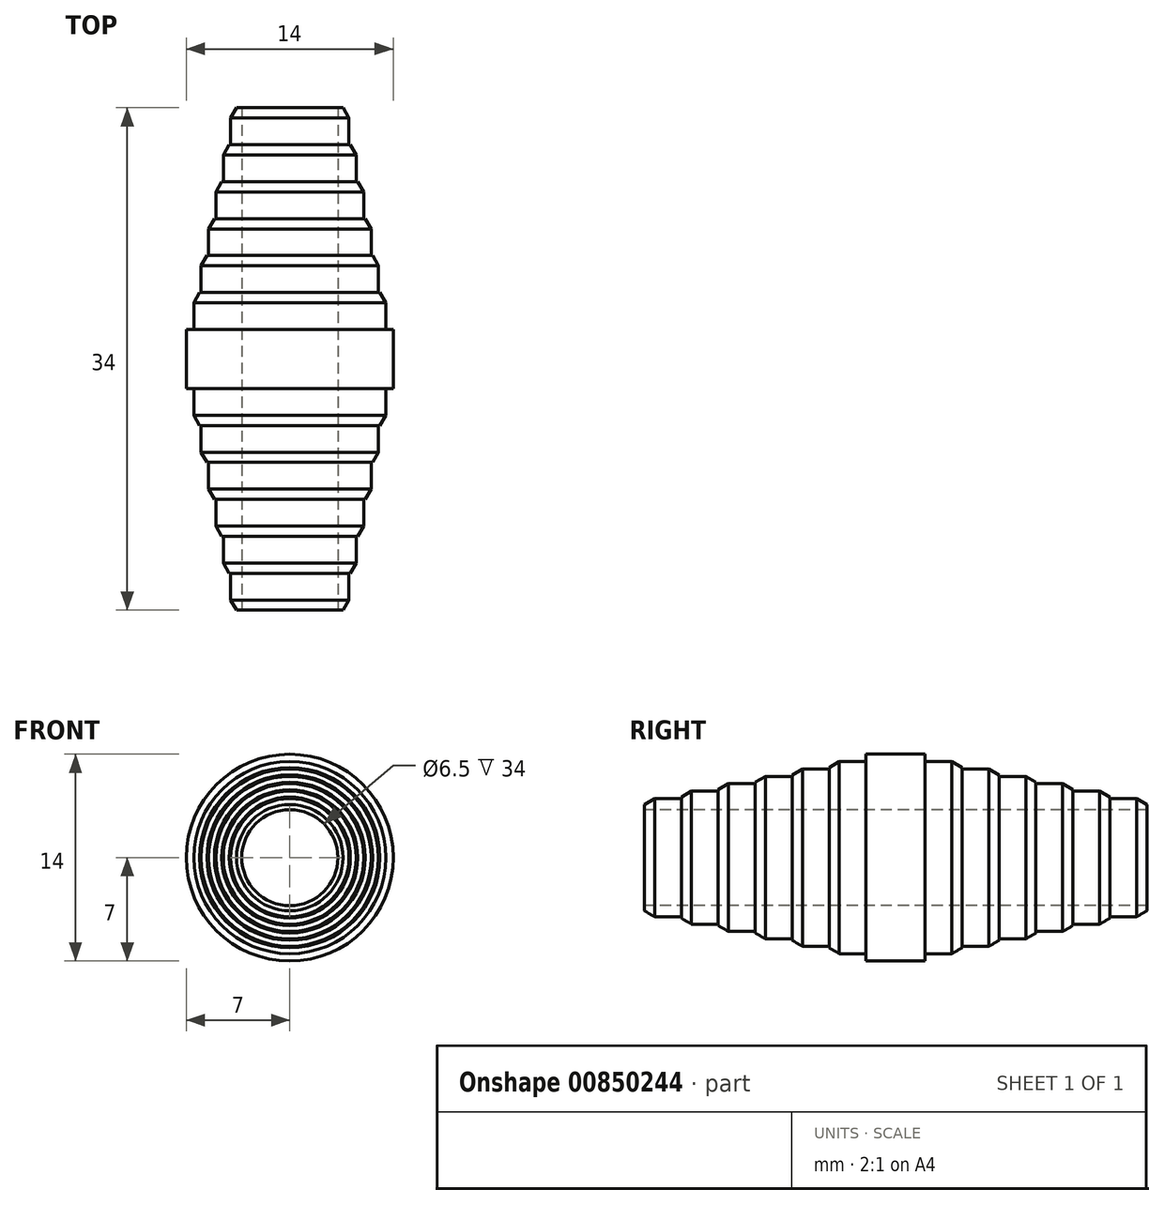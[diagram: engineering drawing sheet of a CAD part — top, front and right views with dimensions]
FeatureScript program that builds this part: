
annotation { "Feature Type Name" : "Feature", "Feature Type Description" : "" }
export const myFeature = defineFeature(function(context is Context, id is Id, definition is map)
    precondition{}
    {
        {
            var Q0;
            Q0=qCreatedBy(makeId("Front.planeOp"),FACE);
            var sketch = newSketch(context, id + "F0", { "sketchPlane" : qUnion([Q0])});
            skCircle(sketch, "E0", {"center": v(0, 0) * mm, "radius": 7 * mm});
            skCircle(sketch, "E1.0", {"center": v(0, 0) * mm, "radius": 6.5 * mm});
            skCircle(sketch, "E2.0", {"center": v(0, 0) * mm, "radius": 6 * mm});
            skCircle(sketch, "E3.0", {"center": v(0, 0) * mm, "radius": 5.5 * mm});
            skCircle(sketch, "E4.0", {"center": v(0, 0) * mm, "radius": 5 * mm});
            skCircle(sketch, "E5.0", {"center": v(0, 0) * mm, "radius": 4.5 * mm});
            skCircle(sketch, "E6.0", {"center": v(0, 0) * mm, "radius": 4 * mm});
            skSolve(sketch);
        }
        {
            var Q0;
            Q0=makeQuery(id+"F0.imprint","IMPRINT",FACE,{"disambiguationData":[TD([[makeQuery(id+"F0.imprint","IMPRINT",EDGE,{"derivedFrom":sQuery(id+"F0.wireOp",EDGE,"E0")}),1.0]])]});
            var Q1;
            Q1=makeQuery(id+"F0.imprint","IMPRINT",FACE,{"disambiguationData":[TD([[makeQuery(id+"F0.imprint","IMPRINT",EDGE,{"derivedFrom":sQuery(id+"F0.wireOp",EDGE,"E1.0")}),1.0]])]});
            var Q2;
            Q2=makeQuery(id+"F0.imprint","IMPRINT",FACE,{"disambiguationData":[TD([[makeQuery(id+"F0.imprint","IMPRINT",EDGE,{"derivedFrom":sQuery(id+"F0.wireOp",EDGE,"E2.0")}),1.0]])]});
            var Q3;
            Q3=makeQuery(id+"F0.imprint","IMPRINT",FACE,{"disambiguationData":[TD([[makeQuery(id+"F0.imprint","IMPRINT",EDGE,{"derivedFrom":sQuery(id+"F0.wireOp",EDGE,"E3.0")}),1.0]])]});
            var Q4;
            Q4=makeQuery(id+"F0.imprint","IMPRINT",FACE,{"disambiguationData":[TD([[makeQuery(id+"F0.imprint","IMPRINT",EDGE,{"derivedFrom":sQuery(id+"F0.wireOp",EDGE,"E4.0")}),1.0]])]});
            var Q5;
            Q5=makeQuery(id+"F0.imprint","IMPRINT",FACE,{"disambiguationData":[TD([[makeQuery(id+"F0.imprint","IMPRINT",EDGE,{"derivedFrom":sQuery(id+"F0.wireOp",EDGE,"E5.0")}),1.0]])]});
            var Q6;
            Q6=makeQuery(id+"F0.imprint","IMPRINT",FACE,{"disambiguationData":[TD([[makeQuery(id+"F0.imprint","IMPRINT",EDGE,{"derivedFrom":sQuery(id+"F0.wireOp",EDGE,"E6.0")}),1.0]])]});
            extrude(context, id + "F1", {"entities" : qUnion([Q0, Q1, Q2, Q3, Q4, Q5, Q6]), "depth" : 2 * mm, "offsetDistance" : 25 * mm});
        }
        {
            var Q0;
            Q0=makeQuery(id+"F0.imprint","IMPRINT",FACE,{"disambiguationData":[TD([[makeQuery(id+"F0.imprint","IMPRINT",EDGE,{"derivedFrom":sQuery(id+"F0.wireOp",EDGE,"E1.0")}),1.0]])]});
            var Q1;
            Q1=makeQuery(id+"F0.imprint","IMPRINT",FACE,{"disambiguationData":[TD([[makeQuery(id+"F0.imprint","IMPRINT",EDGE,{"derivedFrom":sQuery(id+"F0.wireOp",EDGE,"E2.0")}),1.0]])]});
            var Q2;
            Q2=makeQuery(id+"F0.imprint","IMPRINT",FACE,{"disambiguationData":[TD([[makeQuery(id+"F0.imprint","IMPRINT",EDGE,{"derivedFrom":sQuery(id+"F0.wireOp",EDGE,"E3.0")}),1.0]])]});
            var Q3;
            Q3=makeQuery(id+"F0.imprint","IMPRINT",FACE,{"disambiguationData":[TD([[makeQuery(id+"F0.imprint","IMPRINT",EDGE,{"derivedFrom":sQuery(id+"F0.wireOp",EDGE,"E4.0")}),1.0]])]});
            var Q4;
            Q4=makeQuery(id+"F0.imprint","IMPRINT",FACE,{"disambiguationData":[TD([[makeQuery(id+"F0.imprint","IMPRINT",EDGE,{"derivedFrom":sQuery(id+"F0.wireOp",EDGE,"E5.0")}),1.0]])]});
            var Q5;
            Q5=makeQuery(id+"F0.imprint","IMPRINT",FACE,{"disambiguationData":[TD([[makeQuery(id+"F0.imprint","IMPRINT",EDGE,{"derivedFrom":sQuery(id+"F0.wireOp",EDGE,"E6.0")}),1.0]])]});
            var Q6;
            Q6=makeQuery(id+"F1.opExtrude","CAP_FACE",FACE,{"disambiguationData":[OSD([sQuery(id+"F0.wireOp",EDGE,"E0"),sQuery(id+"F0.wireOp",EDGE,"E6.0")])],"isStart":false});
            extrude(context, id + "F2", {"entities" : qUnion([Q0, Q1, Q2, Q3, Q4, Q5]), "operationType" : NewBodyOperationType.ADD, "endBound" : BoundingType.UP_TO_SURFACE, "depth" : 25 * mm, "endBoundEntityFace" : qUnion([Q6]), "hasOffset" : true, "offsetDistance" : -2.5 * mm});
        }
        {
            var Q0;
            Q0=makeQuery(id+"F0.imprint","IMPRINT",FACE,{"disambiguationData":[TD([[makeQuery(id+"F0.imprint","IMPRINT",EDGE,{"derivedFrom":sQuery(id+"F0.wireOp",EDGE,"E6.0")}),1.0]])]});
            var Q1;
            Q1=makeQuery(id+"F0.imprint","IMPRINT",FACE,{"disambiguationData":[TD([[makeQuery(id+"F0.imprint","IMPRINT",EDGE,{"derivedFrom":sQuery(id+"F0.wireOp",EDGE,"E5.0")}),1.0]])]});
            var Q2;
            Q2=makeQuery(id+"F0.imprint","IMPRINT",FACE,{"disambiguationData":[TD([[makeQuery(id+"F0.imprint","IMPRINT",EDGE,{"derivedFrom":sQuery(id+"F0.wireOp",EDGE,"E4.0")}),1.0]])]});
            var Q3;
            Q3=makeQuery(id+"F0.imprint","IMPRINT",FACE,{"disambiguationData":[TD([[makeQuery(id+"F0.imprint","IMPRINT",EDGE,{"derivedFrom":sQuery(id+"F0.wireOp",EDGE,"E3.0")}),1.0]])]});
            var Q4;
            Q4=makeQuery(id+"F0.imprint","IMPRINT",FACE,{"disambiguationData":[TD([[makeQuery(id+"F0.imprint","IMPRINT",EDGE,{"derivedFrom":sQuery(id+"F0.wireOp",EDGE,"E2.0")}),1.0]])]});
            var Q5;
            Q5=makeQuery(id+"F2.opExtrude","CAP_FACE",FACE,{"disambiguationData":[OSD([sQuery(id+"F0.wireOp",EDGE,"E1.0")])],"isStart":false});
            extrude(context, id + "F3", {"entities" : qUnion([Q0, Q1, Q2, Q3, Q4]), "operationType" : NewBodyOperationType.ADD, "endBound" : BoundingType.UP_TO_SURFACE, "depth" : 25 * mm, "endBoundEntityFace" : qUnion([Q5]), "hasOffset" : true, "offsetDistance" : -2.5 * mm});
        }
        {
            var Q0;
            Q0=makeQuery(id+"F0.imprint","IMPRINT",FACE,{"disambiguationData":[TD([[makeQuery(id+"F0.imprint","IMPRINT",EDGE,{"derivedFrom":sQuery(id+"F0.wireOp",EDGE,"E6.0")}),1.0]])]});
            var Q1;
            Q1=makeQuery(id+"F0.imprint","IMPRINT",FACE,{"disambiguationData":[TD([[makeQuery(id+"F0.imprint","IMPRINT",EDGE,{"derivedFrom":sQuery(id+"F0.wireOp",EDGE,"E5.0")}),1.0]])]});
            var Q2;
            Q2=makeQuery(id+"F0.imprint","IMPRINT",FACE,{"disambiguationData":[TD([[makeQuery(id+"F0.imprint","IMPRINT",EDGE,{"derivedFrom":sQuery(id+"F0.wireOp",EDGE,"E4.0")}),1.0]])]});
            var Q3;
            Q3=makeQuery(id+"F0.imprint","IMPRINT",FACE,{"disambiguationData":[TD([[makeQuery(id+"F0.imprint","IMPRINT",EDGE,{"derivedFrom":sQuery(id+"F0.wireOp",EDGE,"E3.0")}),1.0]])]});
            var Q4;
            Q4=makeQuery(id+"F3.opExtrude","CAP_FACE",FACE,{"disambiguationData":[OSD([sQuery(id+"F0.wireOp",EDGE,"E2.0")])],"isStart":false});
            extrude(context, id + "F4", {"entities" : qUnion([Q0, Q1, Q2, Q3]), "operationType" : NewBodyOperationType.ADD, "endBound" : BoundingType.UP_TO_SURFACE, "depth" : 25 * mm, "endBoundEntityFace" : qUnion([Q4]), "hasOffset" : true, "offsetDistance" : -2.5 * mm});
        }
        {
            var Q0;
            Q0=makeQuery(id+"F0.imprint","IMPRINT",FACE,{"disambiguationData":[TD([[makeQuery(id+"F0.imprint","IMPRINT",EDGE,{"derivedFrom":sQuery(id+"F0.wireOp",EDGE,"E6.0")}),1.0]])]});
            var Q1;
            Q1=makeQuery(id+"F0.imprint","IMPRINT",FACE,{"disambiguationData":[TD([[makeQuery(id+"F0.imprint","IMPRINT",EDGE,{"derivedFrom":sQuery(id+"F0.wireOp",EDGE,"E5.0")}),1.0]])]});
            var Q2;
            Q2=makeQuery(id+"F0.imprint","IMPRINT",FACE,{"disambiguationData":[TD([[makeQuery(id+"F0.imprint","IMPRINT",EDGE,{"derivedFrom":sQuery(id+"F0.wireOp",EDGE,"E4.0")}),1.0]])]});
            var Q3;
            Q3=makeQuery(id+"F4.opExtrude","CAP_FACE",FACE,{"disambiguationData":[OSD([sQuery(id+"F0.wireOp",EDGE,"E3.0")])],"isStart":false});
            extrude(context, id + "F5", {"entities" : qUnion([Q0, Q1, Q2]), "operationType" : NewBodyOperationType.ADD, "endBound" : BoundingType.UP_TO_SURFACE, "depth" : 25 * mm, "endBoundEntityFace" : qUnion([Q3]), "hasOffset" : true, "offsetDistance" : -2.5 * mm});
        }
        {
            var Q0;
            Q0=makeQuery(id+"F0.imprint","IMPRINT",FACE,{"disambiguationData":[TD([[makeQuery(id+"F0.imprint","IMPRINT",EDGE,{"derivedFrom":sQuery(id+"F0.wireOp",EDGE,"E6.0")}),1.0]])]});
            var Q1;
            Q1=makeQuery(id+"F0.imprint","IMPRINT",FACE,{"disambiguationData":[TD([[makeQuery(id+"F0.imprint","IMPRINT",EDGE,{"derivedFrom":sQuery(id+"F0.wireOp",EDGE,"E5.0")}),1.0]])]});
            var Q2;
            Q2=makeQuery(id+"F5.opExtrude","CAP_FACE",FACE,{"disambiguationData":[OSD([sQuery(id+"F0.wireOp",EDGE,"E4.0")])],"isStart":false});
            extrude(context, id + "F6", {"entities" : qUnion([Q0, Q1]), "operationType" : NewBodyOperationType.ADD, "endBound" : BoundingType.UP_TO_SURFACE, "depth" : 25 * mm, "endBoundEntityFace" : qUnion([Q2]), "hasOffset" : true, "offsetDistance" : -2.5 * mm});
        }
        {
            var Q0;
            Q0=makeQuery(id+"F0.imprint","IMPRINT",FACE,{"disambiguationData":[TD([[makeQuery(id+"F0.imprint","IMPRINT",EDGE,{"derivedFrom":sQuery(id+"F0.wireOp",EDGE,"E6.0")}),1.0]])]});
            var Q1;
            Q1=makeQuery(id+"F6.opExtrude","CAP_FACE",FACE,{"disambiguationData":[OSD([sQuery(id+"F0.wireOp",EDGE,"E5.0")])],"isStart":false});
            extrude(context, id + "F7", {"entities" : qUnion([Q0]), "operationType" : NewBodyOperationType.ADD, "endBound" : BoundingType.UP_TO_SURFACE, "depth" : 25 * mm, "endBoundEntityFace" : qUnion([Q1]), "hasOffset" : true, "offsetDistance" : -2.5 * mm});
        }
        {
            var Q0;
            Q0=makeQuery(id+"F7.opExtrude","CAP_FACE",FACE,{"disambiguationData":[OSD([sQuery(id+"F0.wireOp",EDGE,"E6.0")])],"isStart":false});
            var sketch = newSketch(context, id + "F8", { "sketchPlane" : qUnion([Q0])});
            skCircle(sketch, "E7.0", {"center": v(0, 0) * mm, "radius": 4 * mm, "construction": true});
            skCircle(sketch, "E8.0", {"center": v(0, 0) * mm, "radius": 3.25 * mm});
            skSolve(sketch);
        }
        {
            var Q0;
            Q0 = qSketchRegion(id + "F8", true);
            var Q1;
            Q1=makeQuery(id+"F1.opExtrude","CAP_FACE",FACE,{"disambiguationData":[OSD([sQuery(id+"F0.wireOp",EDGE,"E0")])],"isStart":true});
            extrude(context, id + "F9", {"entities" : qUnion([Q0]), "operationType" : NewBodyOperationType.REMOVE, "endBound" : BoundingType.UP_TO_SURFACE, "oppositeDirection" : true, "depth" : 25 * mm, "endBoundEntityFace" : qUnion([Q1]), "offsetDistance" : 25 * mm});
        }
        {
            var Q0;
            Q0=makeQuery(id+"F5.opExtrude","CAP_EDGE",EDGE,{"disambiguationData":[OSD([sQuery(id+"F0.wireOp",EDGE,"E4.0")])],"isStart":false});
            var Q1;
            Q1=makeQuery(id+"F4.opExtrude","CAP_EDGE",EDGE,{"disambiguationData":[OSD([sQuery(id+"F0.wireOp",EDGE,"E3.0")])],"isStart":false});
            var Q2;
            Q2=makeQuery(id+"F3.opExtrude","CAP_EDGE",EDGE,{"disambiguationData":[OSD([sQuery(id+"F0.wireOp",EDGE,"E2.0")])],"isStart":false});
            var Q3;
            Q3=makeQuery(id+"F2.opExtrude","CAP_EDGE",EDGE,{"disambiguationData":[OSD([sQuery(id+"F0.wireOp",EDGE,"E1.0")])],"isStart":false});
            var Q4;
            Q4=makeQuery(id+"F6.opExtrude","CAP_EDGE",EDGE,{"disambiguationData":[OSD([sQuery(id+"F0.wireOp",EDGE,"E5.0")])],"isStart":false});
            var Q5;
            Q5=makeQuery(id+"F7.opExtrude","CAP_EDGE",EDGE,{"disambiguationData":[OSD([sQuery(id+"F0.wireOp",EDGE,"E6.0")])],"isStart":false});
            chamfer(context, id + "F10", {"entities" : qUnion([Q0, Q1, Q2, Q3, Q4, Q5]), "chamferType" : ChamferType.OFFSET_ANGLE, "width" : .4 * mm, "oppositeDirection" : false, "angle" : 60 * degree, "tangentPropagation" : true});
        }
        {
            var Q0;
            Q0=makeQuery(id+"F1.opExtrude","SWEPT_BODY",BODY,{"disambiguationData":[OSD([sQuery(id+"F0.wireOp",EDGE,"E0")])]});
            var Q1;
            Q1=qCreatedBy(makeId("Front.planeOp"),FACE);
            mirror(context, id + "F11", {"operationType" : NewBodyOperationType.ADD, "entities" : qUnion([Q0]), "mirrorPlane" : qUnion([Q1])});
        }
    });
